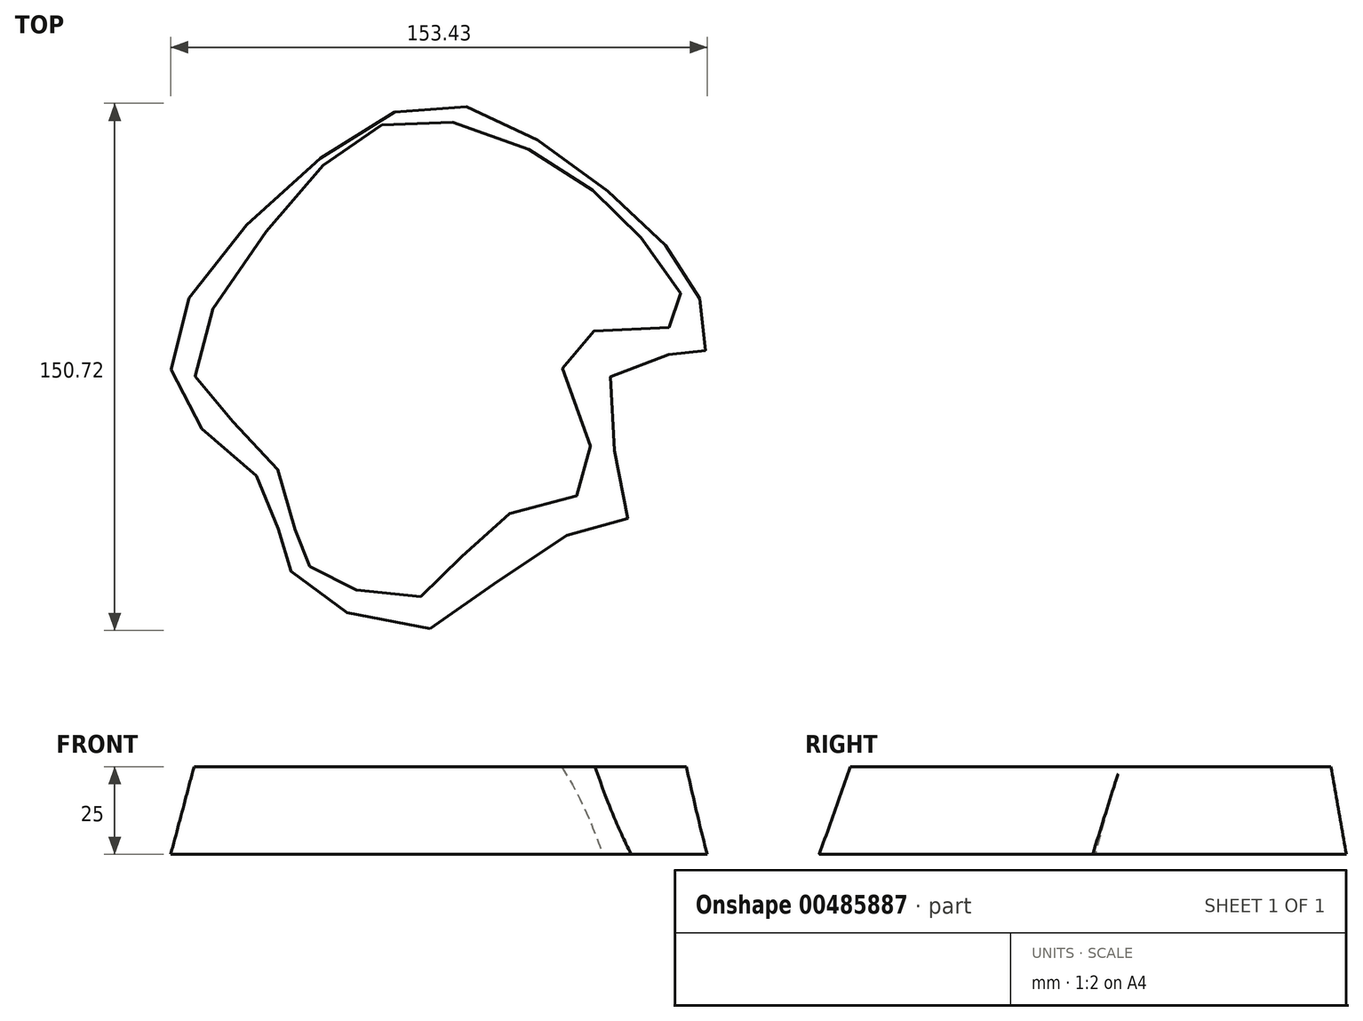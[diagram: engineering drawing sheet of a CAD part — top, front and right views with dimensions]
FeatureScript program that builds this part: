
annotation { "Feature Type Name" : "Feature", "Feature Type Description" : "" }
export const myFeature = defineFeature(function(context is Context, id is Id, definition is map)
    precondition{}
    {
        {
            var Q0;
            Q0=qCreatedBy(makeId("Top.planeOp"),FACE);
            var sketch = newSketch(context, id + "F0", { "sketchPlane" : qUnion([Q0])});
            skFitSpline(sketch, "E0", {"points": [v(-5.67, -78.34) * mm, v(-42.3, -65.31) * mm, v(-48.41, -54.74) * mm, v(-53, -37.65) * mm, v(-74.74, -17.07) * mm, v(-77.77, 9.35) * mm, v(-44.56, 49.7) * mm, v(-6.6, 71.66) * mm, v(25.9, 60.77) * mm, v(58.95, 34.04) * mm, v(72.23, 13.35) * mm, v(72.23, 0) * mm, v(62.5, 0) * mm, v(43.86, -10.63) * mm, v(51.43, -45.74) * mm, v(28.37, -53.41) * mm, v(-5.67, -78.34) * mm]});
            skSolve(sketch);
        }
        {
            var Q0;
            Q0=qCreatedBy(makeId("Top.planeOp"),FACE);
            cPlane(context, id + "F1", {"entities" : qUnion([Q0]), "cplaneType" : CPlaneType.OFFSET, "offset" : 25 * mm, "width" : 150 * mm, "height" : 150 * mm});
        }
        {
            var Q0;
            Q0=qCreatedBy(id+"F1.planeOp",FACE);
            var sketch = newSketch(context, id + "F2", { "sketchPlane" : qUnion([Q0])});
            skFitSpline(sketch, "E1.0", {"points": [v(-5.67, -78.34) * mm, v(-18.2, -81.27) * mm, v(-44.24, -66.67) * mm, v(-49.22, -55.38) * mm, v(-49.34, -34.61) * mm, v(-79.2, -19.65) * mm, v(-82.83, 12.7) * mm, v(-45.62, 50.68) * mm, v(-7.73, 78.64) * mm, v(26.94, 61.99) * mm, v(59.63, 35.53) * mm, v(73.36, 16.07) * mm, v(74.47, -3.31) * mm, v(62.25, 2.12) * mm, v(32.48, -6.66) * mm, v(63.69, -53.9) * mm, v(22.42, -46.48) * mm, v(7.38, -75.29) * mm, v(-5.67, -78.34) * mm], "construction": true});
            skFitSpline(sketch, "E2", {"points": [v(-36.4, -63.12) * mm, v(-43.22, -55.23) * mm, v(-51.62, -28.98) * mm, v(-72.82, -6.58) * mm, v(-48.66, 39.98) * mm, v(-14, 67.02) * mm, v(30.86, 53.93) * mm, v(58.95, 28.02) * mm, v(65.92, 8.9) * mm, v(32.85, 3.12) * mm, v(41.14, -35.37) * mm, v(12.95, -47.4) * mm, v(-7.01, -68.76) * mm, v(-36.4, -63.12) * mm]});
            skSolve(sketch);
        }
        {
            var Q0;
            Q0=makeQuery(id+"F0.imprint","IMPRINT",FACE,{"disambiguationData":[TD([[makeQuery(id+"F0.imprint","IMPRINT",EDGE,{"derivedFrom":sQuery(id+"F0.wireOp",EDGE,"E0")}),-1.0]])]});
            var Q1;
            Q1=makeQuery(id+"F2.imprint","IMPRINT",FACE,{"disambiguationData":[TD([[makeQuery(id+"F2.imprint","IMPRINT",EDGE,{"derivedFrom":sQuery(id+"F2.wireOp",EDGE,"E2")}),-1.0]])]});
            loft(context, id + "F3", {"sheetProfilesArray" : [{ "sheetProfileEntities" : qUnion([Q0]) }, { "sheetProfileEntities" : qUnion([Q1]) }]});
        }
    });
